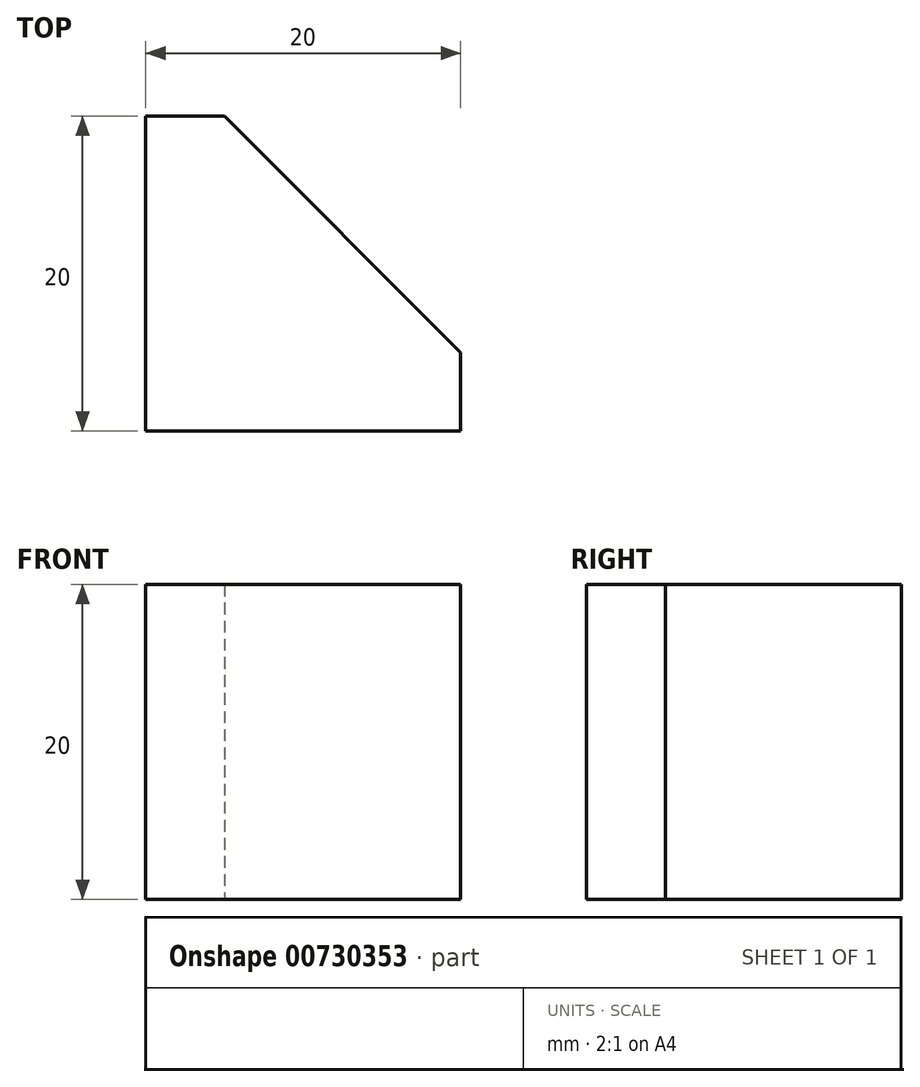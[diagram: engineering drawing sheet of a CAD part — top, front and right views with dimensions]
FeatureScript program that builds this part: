
annotation { "Feature Type Name" : "Feature", "Feature Type Description" : "" }
export const myFeature = defineFeature(function(context is Context, id is Id, definition is map)
    precondition{}
    {
        {
            var Q0;
            Q0=qCreatedBy(makeId("Top.planeOp"),FACE);
            var sketch = newSketch(context, id + "F0", { "sketchPlane" : qUnion([Q0])});
            skLineSegment(sketch, "E0.bottom", {"start": v(0, 0) * mm, "end": v(20, 0) * mm});
            skLineSegment(sketch, "E0.top", {"start": v(0, 20) * mm, "end": v(5, 20) * mm});
            skLineSegment(sketch, "E0.left", {"start": v(0, 0) * mm, "end": v(0, 20) * mm});
            skLineSegment(sketch, "E0.right", {"start": v(20, 0) * mm, "end": v(20, 5) * mm});
            skLineSegment(sketch, "E1", {"start": v(5, 20) * mm, "end": v(20, 5) * mm});
            skSolve(sketch);
        }
        {
            var Q0;
            Q0 = qSketchRegion(id + "F0", true);
            extrude(context, id + "F1", {"entities" : qUnion([Q0]), "depth" : 20 * mm, "offsetDistance" : 25 * mm});
        }
    });
